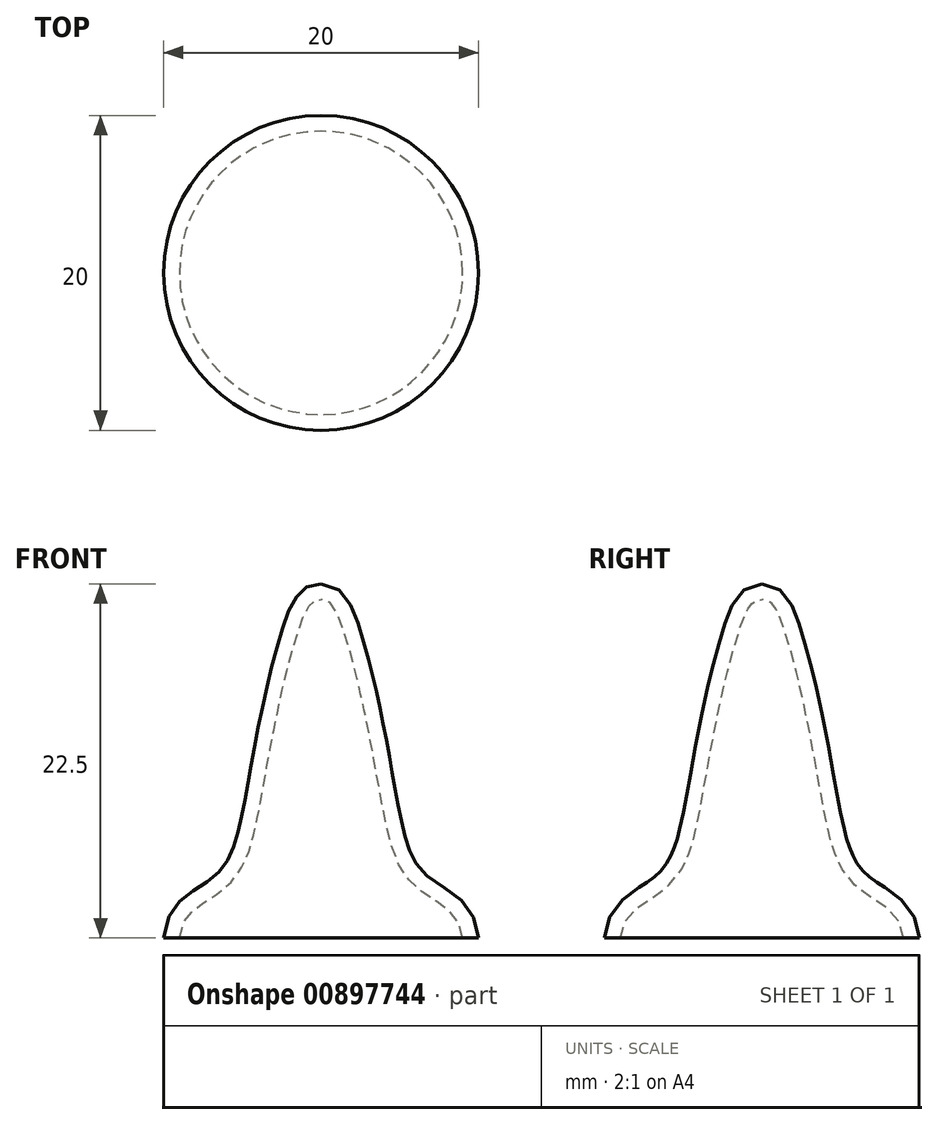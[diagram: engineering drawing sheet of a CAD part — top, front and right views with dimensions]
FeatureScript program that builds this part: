
annotation { "Feature Type Name" : "Feature", "Feature Type Description" : "" }
export const myFeature = defineFeature(function(context is Context, id is Id, definition is map)
    precondition{}
    {
        {
            var Q0;
            Q0=qCreatedBy(makeId("Front.planeOp"),FACE);
            var sketch = newSketch(context, id + "F0", { "sketchPlane" : qUnion([Q0])});
            skLineSegment(sketch, "E0", {"start": v(0, 0.05) * mm, "end": v(0, 30) * mm});
            skEllipticalArc(sketch, "E1", {});
            skFitSpline(sketch, "E2", {"points": [v(-10, 7.5) * mm, v(-6.69, 11.5) * mm, v(-5.1, 14.95) * mm, v(-4.1, 20.28) * mm, v(-2.44, 27.2) * mm, v(0, 30) * mm], "startDerivative": vector(2.9, 37.54) * mm, "endDerivative": vector(24.45, -0.45) * mm});
            skPoint(sketch, "E3.orphan", {"position": v(10, 7.5) * mm});
            skLineSegment(sketch, "E4", {"start": v(-1.2, 0.05) * mm, "end": v(0, 0.05) * mm});
            skPoint(sketch, "E5.orphan", {"position": v(0, 0) * mm});
            const initialGuessF0  = {"E1": [0, 0.0075, 1, 0, 0.01, 0.0075, 3.141592653589793, 4.592936546162219]};
            skSetInitialGuess(sketch, initialGuessF0);
            skSolve(sketch);
        }
        {
            var Q0;
            Q0=makeQuery(id+"F0.imprint","IMPRINT",FACE,{"disambiguationData":[TD([[makeQuery(id+"F0.imprint","IMPRINT",EDGE,{"derivedFrom":sQuery(id+"F0.wireOp",EDGE,"E0")}),1.0]])]});
            var Q1;
            Q1=sQuery(id+"F0.wireOp",EDGE,"E0");
            revolve(context, id + "F1", {"surfaceOperationType" : NewSurfaceOperationType.NEW, "entities" : qUnion([Q0]), "axis" : qUnion([Q1]), "revolveType" : RevolveType.FULL});
        }
        {
            var Q0;
            Q0=qCreatedBy(makeId("Front.planeOp"),FACE);
            var sketch = newSketch(context, id + "F2", { "sketchPlane" : qUnion([Q0])});
            skLineSegment(sketch, "E6.bottom", {"start": v(0, 0) * mm, "end": v(22.7, 0) * mm});
            skLineSegment(sketch, "E6.top", {"start": v(0, 7.5) * mm, "end": v(22.7, 7.5) * mm});
            skLineSegment(sketch, "E6.left", {"start": v(0, 0) * mm, "end": v(0, 7.5) * mm});
            skLineSegment(sketch, "E6.right", {"start": v(22.7, 0) * mm, "end": v(22.7, 7.5) * mm});
            skSolve(sketch);
        }
        {
            var Q0;
            Q0=makeQuery(id+"F2.imprint","IMPRINT",FACE,{"disambiguationData":[TD([[makeQuery(id+"F2.imprint","IMPRINT",EDGE,{"derivedFrom":sQuery(id+"F2.wireOp",EDGE,"E6.bottom")}),1.0]])]});
            var Q1;
            Q1=sQuery(id+"F2.wireOp",EDGE,"E6.left");
            revolve(context, id + "F3", {"operationType" : NewBodyOperationType.REMOVE, "surfaceOperationType" : NewSurfaceOperationType.NEW, "entities" : qUnion([Q0]), "axis" : qUnion([Q1]), "revolveType" : RevolveType.FULL, "oppositeDirection" : true});
        }
        {
            var Q0;
            Q0=makeQuery(id+"F3.boolean.opBoolean","COPY",FACE,{"derivedFrom":makeQuery(id+"F3.opRevolve","SWEPT_FACE",FACE,{"disambiguationData":[OSD([sQuery(id+"F2.wireOp",EDGE,"E6.top")])]})});
            shell(context, id + "F4", {"entities" : qUnion([Q0]), "thickness" : 1 * mm});
        }
    });
